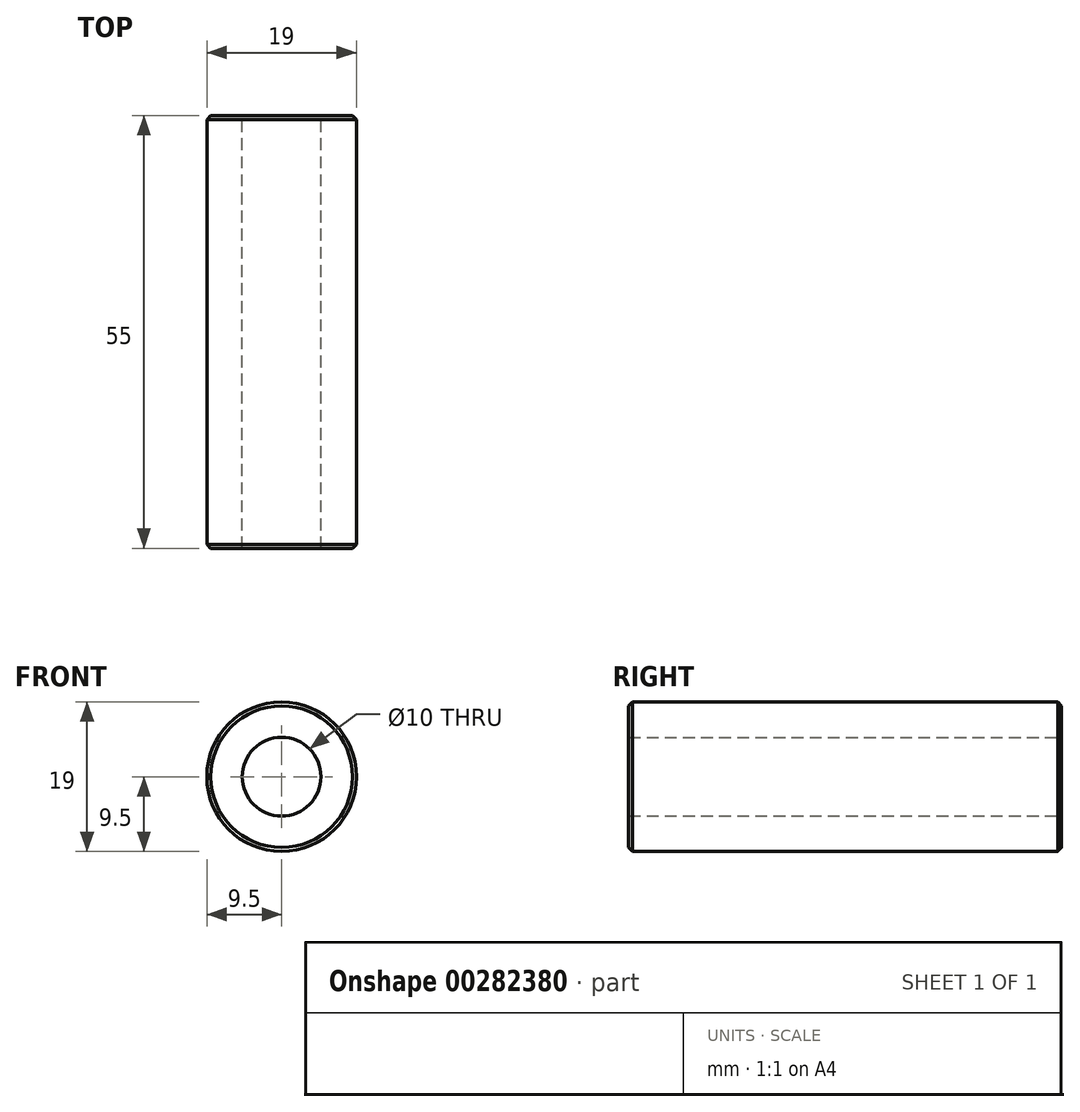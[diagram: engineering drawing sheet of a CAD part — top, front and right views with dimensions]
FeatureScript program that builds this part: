
annotation { "Feature Type Name" : "Feature", "Feature Type Description" : "" }
export const myFeature = defineFeature(function(context is Context, id is Id, definition is map)
    precondition{}
    {
        {
            var Q0;
            Q0=qCreatedBy(makeId("Front.planeOp"),FACE);
            var sketch = newSketch(context, id + "F0", { "sketchPlane" : qUnion([Q0])});
            skCircle(sketch, "E0", {"center": v(0, 0) * mm, "radius": 5 * mm});
            skCircle(sketch, "E1", {"center": v(0, 0) * mm, "radius": 9.5 * mm});
            skSolve(sketch);
        }
        {
            var Q0;
            Q0=qSketchRegion(id+"F0",true);
            extrude(context, id + "F1", {"entities" : qUnion([Q0]), "depth" : 55 * mm});
        }
        {
            var Q0;
            Q0=makeQuery(id+"F1.opExtrude","CAP_EDGE",EDGE,{"disambiguationData":[OSD([sQuery(id+"F0.wireOp",EDGE,"E1")])],"isStart":false});
            var Q1;
            Q1=makeQuery(id+"F1.opExtrude","CAP_EDGE",EDGE,{"disambiguationData":[OSD([sQuery(id+"F0.wireOp",EDGE,"E1")])],"isStart":true});
            chamfer(context, id + "F2", {"entities" : qUnion([Q0, Q1]), "width" : 0.5 * mm, "tangentPropagation" : true});
        }
    });
